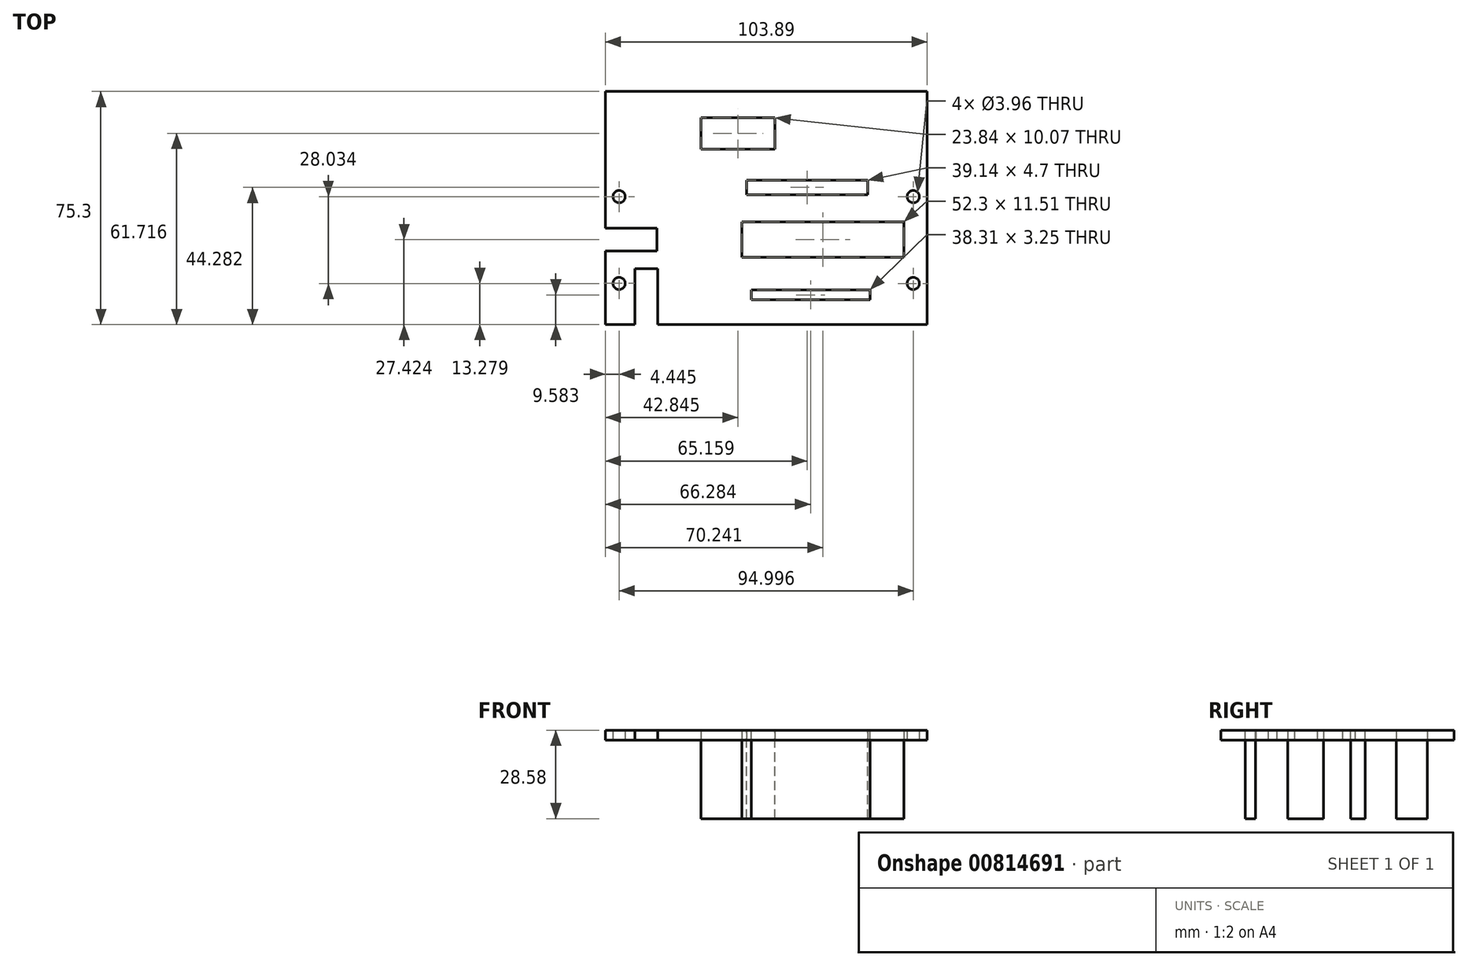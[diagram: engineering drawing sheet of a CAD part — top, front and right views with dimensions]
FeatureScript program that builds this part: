
annotation { "Feature Type Name" : "Feature", "Feature Type Description" : "" }
export const myFeature = defineFeature(function(context is Context, id is Id, definition is map)
    precondition{}
    {
        {
            var Q0;
            Q0=qCreatedBy(makeId("Top.planeOp"),FACE);
            var sketch = newSketch(context, id + "F0", { "sketchPlane" : qUnion([Q0])});
            skLineSegment(sketch, "E0.bottom", {"start": v(0, 0) * mm, "end": v(103.89, 0) * mm});
            skLineSegment(sketch, "E0.top", {"start": v(0, 75.3) * mm, "end": v(103.89, 75.3) * mm});
            skLineSegment(sketch, "E0.left", {"start": v(0, 0) * mm, "end": v(0, 75.3) * mm});
            skLineSegment(sketch, "E0.right", {"start": v(103.89, 0) * mm, "end": v(103.89, 75.3) * mm});
            skLineSegment(sketch, "E1.bottom", {"start": v(9.52, 0) * mm, "end": v(16.89, 0) * mm});
            skLineSegment(sketch, "E1.top", {"start": v(9.52, 18.03) * mm, "end": v(16.89, 18.03) * mm});
            skLineSegment(sketch, "E1.left", {"start": v(9.52, 0) * mm, "end": v(9.52, 18.03) * mm});
            skLineSegment(sketch, "E1.right", {"start": v(16.89, 0) * mm, "end": v(16.89, 18.03) * mm});
            skLineSegment(sketch, "E2.bottom", {"start": v(0, 31.1) * mm, "end": v(16.64, 31.1) * mm});
            skLineSegment(sketch, "E2.top", {"start": v(0, 23.74) * mm, "end": v(16.64, 23.74) * mm});
            skLineSegment(sketch, "E2.left", {"start": v(0, 31.1) * mm, "end": v(0, 23.74) * mm});
            skLineSegment(sketch, "E2.right", {"start": v(16.64, 31.1) * mm, "end": v(16.64, 23.74) * mm});
            skLineSegment(sketch, "E3.bottom", {"start": v(30.93, 66.75) * mm, "end": v(54.76, 66.75) * mm});
            skLineSegment(sketch, "E3.top", {"start": v(30.93, 56.68) * mm, "end": v(54.76, 56.68) * mm});
            skLineSegment(sketch, "E3.left", {"start": v(30.93, 66.75) * mm, "end": v(30.93, 56.68) * mm});
            skLineSegment(sketch, "E3.right", {"start": v(54.76, 66.75) * mm, "end": v(54.76, 56.68) * mm});
            skLineSegment(sketch, "E4.bottom", {"start": v(45.59, 46.63) * mm, "end": v(84.73, 46.63) * mm});
            skLineSegment(sketch, "E4.top", {"start": v(45.59, 41.93) * mm, "end": v(84.73, 41.93) * mm});
            skLineSegment(sketch, "E4.left", {"start": v(45.59, 46.63) * mm, "end": v(45.59, 41.93) * mm});
            skLineSegment(sketch, "E4.right", {"start": v(84.73, 46.63) * mm, "end": v(84.73, 41.93) * mm});
            skLineSegment(sketch, "E5.bottom", {"start": v(44.09, 33.18) * mm, "end": v(96.4, 33.18) * mm});
            skLineSegment(sketch, "E5.top", {"start": v(44.09, 21.67) * mm, "end": v(96.4, 21.67) * mm});
            skLineSegment(sketch, "E5.left", {"start": v(44.09, 33.18) * mm, "end": v(44.09, 21.67) * mm});
            skLineSegment(sketch, "E5.right", {"start": v(96.4, 33.18) * mm, "end": v(96.4, 21.67) * mm});
            skLineSegment(sketch, "E6.bottom", {"start": v(47.13, 11.2) * mm, "end": v(85.44, 11.2) * mm});
            skLineSegment(sketch, "E6.top", {"start": v(47.13, 7.96) * mm, "end": v(85.44, 7.96) * mm});
            skLineSegment(sketch, "E6.left", {"start": v(47.13, 11.2) * mm, "end": v(47.13, 7.96) * mm});
            skLineSegment(sketch, "E6.right", {"start": v(85.44, 11.2) * mm, "end": v(85.44, 7.96) * mm});
            skCircle(sketch, "E7", {"center": v(99.44, 13.28) * mm, "radius": 1.98 * mm});
            skCircle(sketch, "E8", {"center": v(99.44, 41.31) * mm, "radius": 1.98 * mm});
            skCircle(sketch, "E9", {"center": v(4.44, 41.31) * mm, "radius": 1.98 * mm});
            skCircle(sketch, "E10", {"center": v(4.45, 13.28) * mm, "radius": 1.98 * mm});
            skSolve(sketch);
        }
        {
            var Q0;
            Q0=makeQuery(id+"F0.imprint","IMPRINT",FACE,{"disambiguationData":[TD([[makeQuery(id+"F0.imprint","IMPRINT",EDGE,{"derivedFrom":sQuery(id+"F0.wireOp",EDGE,"E5.bottom")}),-1.0]])]});
            var Q1;
            Q1=makeQuery(id+"F0.imprint","IMPRINT",FACE,{"disambiguationData":[TD([[makeQuery(id+"F0.imprint","IMPRINT",EDGE,{"derivedFrom":sQuery(id+"F0.wireOp",EDGE,"E6.bottom")}),-1.0]])]});
            var Q2;
            Q2=makeQuery(id+"F0.imprint","IMPRINT",FACE,{"disambiguationData":[TD([[makeQuery(id+"F0.imprint","IMPRINT",EDGE,{"derivedFrom":sQuery(id+"F0.wireOp",EDGE,"E4.bottom")}),-1.0]])]});
            var Q3;
            Q3=makeQuery(id+"F0.imprint","IMPRINT",FACE,{"disambiguationData":[TD([[makeQuery(id+"F0.imprint","IMPRINT",EDGE,{"derivedFrom":sQuery(id+"F0.wireOp",EDGE,"E3.bottom")}),-1.0]])]});
            extrude(context, id + "F1", {"entities" : qUnion([Q0, Q1, Q2, Q3]), "depth" : -25.4 * mm, "offsetDistance" : 25.4 * mm, "hasSecondDirection" : true, "secondDirectionOppositeDirection" : false, "secondDirectionDepth" : 3.17 * mm});
        }
        {
            var Q0;
            {var subQ5=sQuery(id+"F0.wireOp",EDGE,"E0.top");Q0=makeQuery(id+"F0.imprint","IMPRINT",FACE,{"disambiguationData":[TD([[makeQuery(id+"F0.imprint","IMPRINT",EDGE,{"derivedFrom":subQ5}),-1.0]])]});}
            extrude(context, id + "F2", {"entities" : qUnion([Q0]), "depth" : 3.17 * mm, "offsetDistance" : 25.4 * mm});
        }
    });
